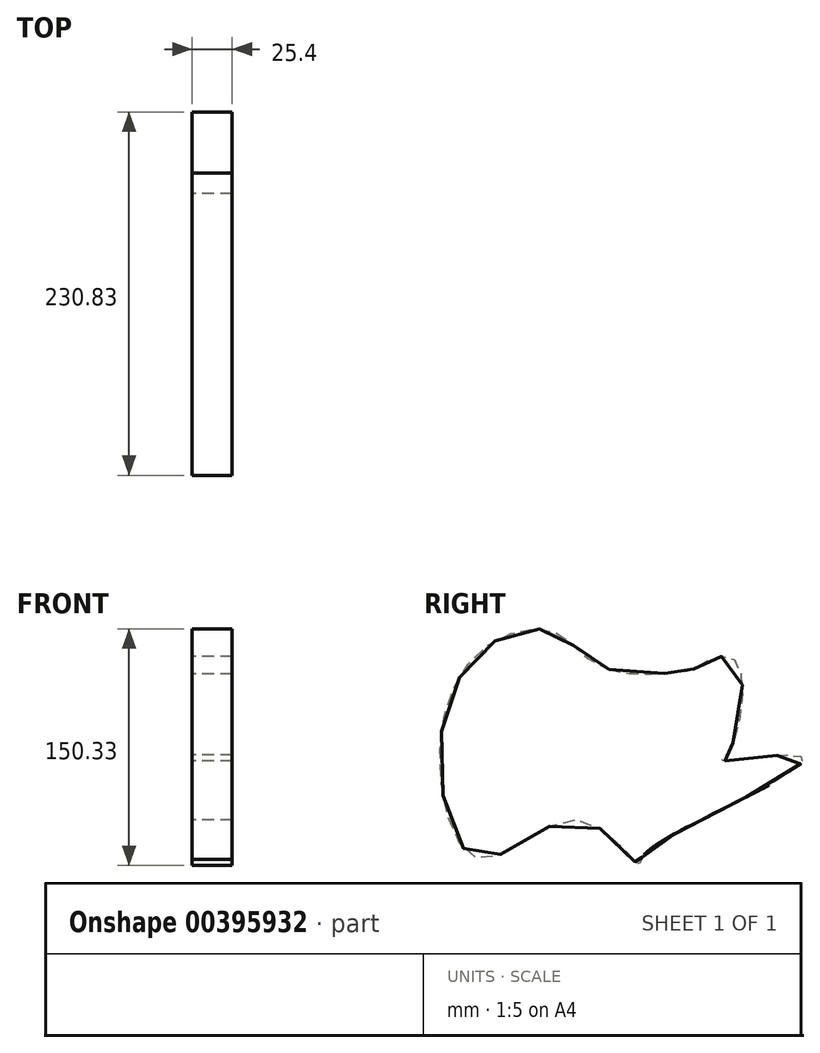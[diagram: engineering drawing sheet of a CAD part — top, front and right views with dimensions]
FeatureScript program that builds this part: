
annotation { "Feature Type Name" : "Feature", "Feature Type Description" : "" }
export const myFeature = defineFeature(function(context is Context, id is Id, definition is map)
    precondition{}
    {
        {
            var Q0;
            Q0=qCreatedBy(makeId("Right.planeOp"),FACE);
            var sketch = newSketch(context, id + "F0", { "sketchPlane" : qUnion([Q0])});
            skFitSpline(sketch, "E0", {"points": [v(0, 41.7) * mm, v(-51.4, 5.59) * mm, v(36.55, -45.65) * mm, v(47.4, -17.44) * mm, v(0, 41.7) * mm]});
            skFitSpline(sketch, "E1", {"points": [v(-56.54, 67.51) * mm, v(0, 20.34) * mm, v(59.4, -37.94) * mm, v(36.55, -59.5) * mm, v(-29.13, 12.59) * mm, v(-62.83, 28.12) * mm, v(-56.54, 67.51) * mm]});
            skSolve(sketch);
        }
        {
            var Q0;
            {var subQ0=sQuery(id+"F0.wireOp",EDGE,"E1");var subQ1=sQuery(id+"F0.wireOp",EDGE,"E0");var subQ2=makeQuery(id+"F0.imprint","INTERSECT",VERTEX,{"disambiguationData":[OD(0.0)],"derivedFrom":[subQ1,subQ0]});Q0=makeQuery(id+"F0.imprint","IMPRINT",FACE,{"disambiguationData":[TD([[makeQuery(id+"F0.imprint","IMPRINT",EDGE,{"disambiguationData":[TD([[subQ2,1.0]])],"derivedFrom":subQ1}),1.0]])]});}
            var Q1;
            {var subQ0=sQuery(id+"F0.wireOp",EDGE,"E1");var subQ1=sQuery(id+"F0.wireOp",EDGE,"E0");var subQ2=makeQuery(id+"F0.imprint","INTERSECT",VERTEX,{"disambiguationData":[OD(1.0)],"derivedFrom":[subQ1,subQ0]});Q1=makeQuery(id+"F0.imprint","IMPRINT",FACE,{"disambiguationData":[TD([[makeQuery(id+"F0.imprint","IMPRINT",EDGE,{"disambiguationData":[TD([[subQ2,1.0]])],"derivedFrom":subQ1}),1.0]])]});}
            var Q2;
            {var subQ0=sQuery(id+"F0.wireOp",EDGE,"E1");var subQ1=sQuery(id+"F0.wireOp",EDGE,"E0");var subQ2=makeQuery(id+"F0.imprint","INTERSECT",VERTEX,{"disambiguationData":[OD(0.0)],"derivedFrom":[subQ1,subQ0]});Q2=makeQuery(id+"F0.imprint","IMPRINT",FACE,{"disambiguationData":[TD([[makeQuery(id+"F0.imprint","IMPRINT",EDGE,{"disambiguationData":[TD([[subQ2,1.0]])],"derivedFrom":subQ1}),-1.0]])]});}
            var Q3;
            {var subQ0=sQuery(id+"F0.wireOp",EDGE,"E1");var subQ1=sQuery(id+"F0.wireOp",EDGE,"E0");var subQ2=makeQuery(id+"F0.imprint","INTERSECT",VERTEX,{"disambiguationData":[OD(0.0)],"derivedFrom":[subQ1,subQ0]});Q3=makeQuery(id+"F0.imprint","IMPRINT",FACE,{"disambiguationData":[TD([[makeQuery(id+"F0.imprint","IMPRINT",EDGE,{"disambiguationData":[TD([[subQ2,-1.0]])],"derivedFrom":subQ1}),1.0]])]});}
            extrude(context, id + "F1", {"entities" : qUnion([Q0, Q1, Q2, Q3]), "depth" : 25.4 * mm});
        }
        {
            var Q0;
            Q0=qCreatedBy(makeId("Right.planeOp"),FACE);
            var sketch = newSketch(context, id + "F2", { "sketchPlane" : qUnion([Q0])});
            skFitSpline(sketch, "E2", {"points": [v(2.93, 49.32) * mm, v(56.25, 49.36) * mm, v(57.12, 49.92) * mm, v(81.43, 56.56) * mm, v(78.64, -3.7) * mm, v(75.1, -8.53) * mm, v(125.95, -6.59) * mm, v(38.23, -58.69) * mm, v(22.8, -73.06) * mm, v(22.3, -75.12) * mm, v(-15.33, -46.41) * mm, v(-77.53, -71.04) * mm, v(-104.36, -12.12) * mm, v(-78.63, 61.08) * mm, v(-31.5, 73.12) * mm, v(2.93, 49.32) * mm]});
            skSolve(sketch);
        }
        {
            var Q0;
            Q0=makeQuery(id+"F2.imprint","IMPRINT",FACE,{"disambiguationData":[TD([[makeQuery(id+"F2.imprint","IMPRINT",EDGE,{"derivedFrom":sQuery(id+"F2.wireOp",EDGE,"E2")}),-1.0]])]});
            extrude(context, id + "F3", {"entities" : qUnion([Q0]), "operationType" : NewBodyOperationType.ADD, "depth" : 25.4 * mm});
        }
    });
